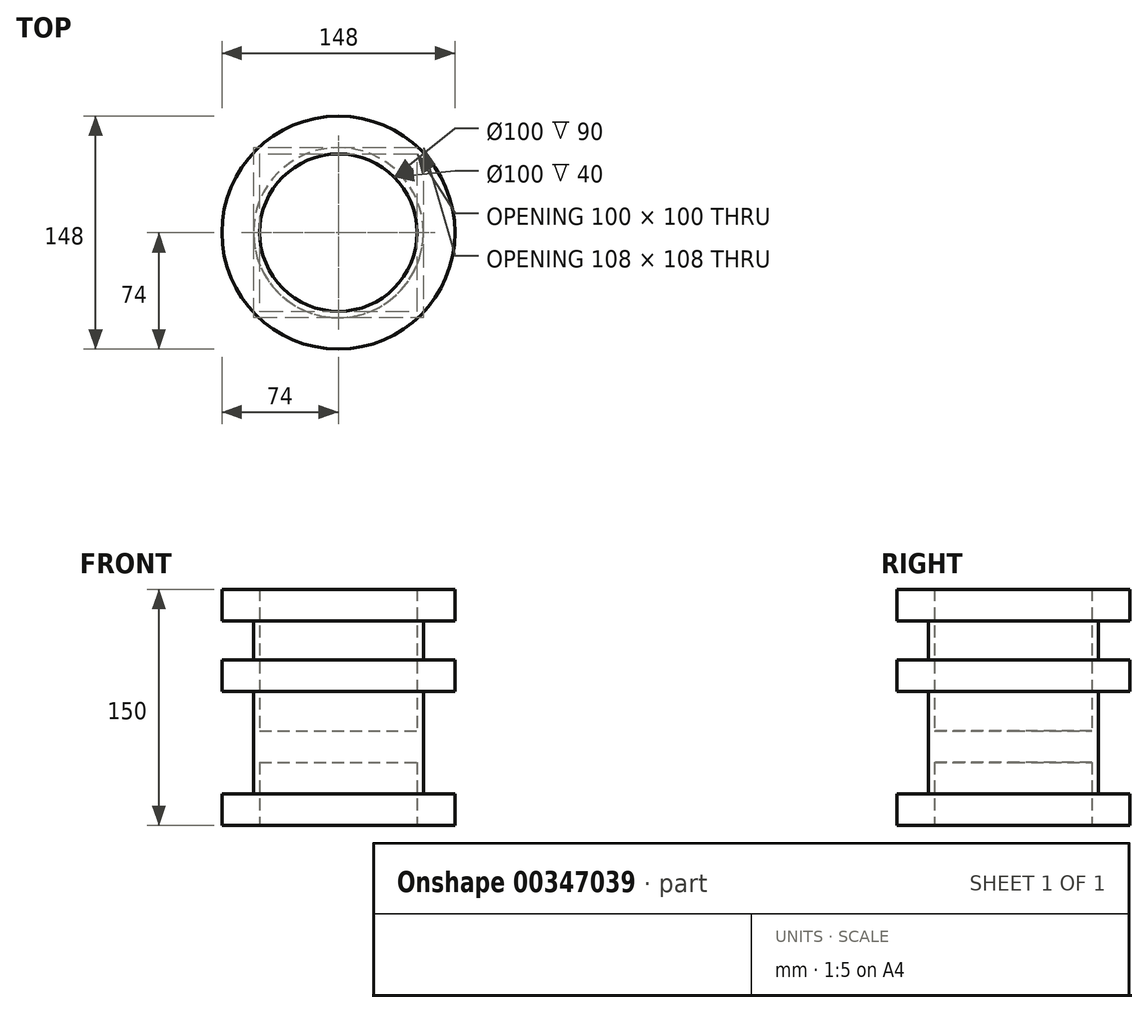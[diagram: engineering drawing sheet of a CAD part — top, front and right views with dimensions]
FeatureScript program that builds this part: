
annotation { "Feature Type Name" : "Feature", "Feature Type Description" : "" }
export const myFeature = defineFeature(function(context is Context, id is Id, definition is map)
    precondition{}
    {
        {
            var Q0;
            Q0=qCreatedBy(makeId("Top.planeOp"),FACE);
            var sketch = newSketch(context, id + "F0", { "sketchPlane" : qUnion([Q0])});
            skCircle(sketch, "E0", {"center": v(0, 0) * mm, "radius": 50 * mm});
            skCircle(sketch, "E1.0", {"center": v(0, 0) * mm, "radius": 54 * mm});
            skSolve(sketch);
        }
        {
            var Q0;
            Q0 = qSketchRegion(id + "F0", true);
            extrude(context, id + "F1", {"entities" : qUnion([Q0]), "depth" : 150 * mm});
        }
        {
            var Q0;
            Q0=qCreatedBy(makeId("Top.planeOp"),FACE);
            var sketch = newSketch(context, id + "F2", { "sketchPlane" : qUnion([Q0])});
            skCircle(sketch, "E2.0", {"center": v(0, 0) * mm, "radius": 54 * mm});
            skCircle(sketch, "E3.0", {"center": v(0, 0) * mm, "radius": 74 * mm});
            skSolve(sketch);
        }
        {
            var Q0;
            Q0=makeQuery(id+"F2.imprint","IMPRINT",FACE,{"disambiguationData":[TD([[makeQuery(id+"F2.imprint","IMPRINT",EDGE,{"derivedFrom":sQuery(id+"F2.wireOp",EDGE,"E2.0")}),-1.0]])]});
            extrude(context, id + "F3", {"entities" : qUnion([Q0]), "operationType" : NewBodyOperationType.ADD, "depth" : 20 * mm});
        }
        {
            var Q0;
            Q0=makeQuery(id+"F1.opExtrude","CAP_FACE",FACE,{"disambiguationData":[OSD([sQuery(id+"F0.wireOp",EDGE,"E0"),sQuery(id+"F0.wireOp",EDGE,"E1.0")])],"isStart":false});
            var sketch = newSketch(context, id + "F4", { "sketchPlane" : qUnion([Q0])});
            skCircle(sketch, "E4.0", {"center": v(0, 0) * mm, "radius": 54 * mm});
            skCircle(sketch, "E5.0", {"center": v(0, 0) * mm, "radius": 74 * mm});
            skSolve(sketch);
        }
        {
            var Q0;
            Q0=makeQuery(id+"F4.imprint","IMPRINT",FACE,{"disambiguationData":[TD([[makeQuery(id+"F4.imprint","IMPRINT",EDGE,{"derivedFrom":sQuery(id+"F4.wireOp",EDGE,"E4.0")}),-1.0]])]});
            extrude(context, id + "F5", {"entities" : qUnion([Q0]), "operationType" : NewBodyOperationType.ADD, "oppositeDirection" : true, "depth" : 20 * mm});
        }
        {
            var Q0;
            Q0=makeQuery(id+"F5.opExtrude","CAP_FACE",FACE,{"disambiguationData":[OSD([sQuery(id+"F4.wireOp",EDGE,"E4.0"),sQuery(id+"F4.wireOp",EDGE,"E5.0")])],"isStart":false});
            cPlane(context, id + "F6", {"entities" : qUnion([Q0]), "cplaneType" : CPlaneType.OFFSET, "offset" : 25 * mm, "width" : 150 * mm, "height" : 150 * mm});
        }
        {
            var Q0;
            Q0=qCreatedBy(id+"F6.planeOp",FACE);
            var sketch = newSketch(context, id + "F7", { "sketchPlane" : qUnion([Q0])});
            skCircle(sketch, "E6.0", {"center": v(0, 0) * mm, "radius": 54 * mm});
            skCircle(sketch, "E6.1", {"center": v(0, 0) * mm, "radius": 74 * mm});
            skSolve(sketch);
        }
        {
            var Q0;
            Q0 = qSketchRegion(id + "F7", true);
            extrude(context, id + "F8", {"entities" : qUnion([Q0]), "operationType" : NewBodyOperationType.ADD, "depth" : 20 * mm});
        }
        {
            var Q0;
            Q0=makeQuery(id+"F8.opExtrude","CAP_FACE",FACE,{"disambiguationData":[OSD([sQuery(id+"F7.wireOp",EDGE,"E6.0"),sQuery(id+"F7.wireOp",EDGE,"E6.1")])],"isStart":false});
            cPlane(context, id + "F9", {"entities" : qUnion([Q0]), "cplaneType" : CPlaneType.OFFSET, "offset" : 25 * mm, "width" : 150 * mm, "height" : 150 * mm});
        }
        {
            var Q0;
            Q0=qCreatedBy(id+"F9.planeOp",FACE);
            var sketch = newSketch(context, id + "F10", { "sketchPlane" : qUnion([Q0])});
            skCircle(sketch, "E7.0", {"center": v(0, 0) * mm, "radius": 54 * mm});
            skCircle(sketch, "E7.1", {"center": v(0, 0) * mm, "radius": 74 * mm});
            skSolve(sketch);
        }
        {
            var Q0;
            Q0=makeQuery(id+"F10.imprint","IMPRINT",FACE,{"disambiguationData":[TD([[makeQuery(id+"F10.imprint","IMPRINT",EDGE,{"derivedFrom":sQuery(id+"F10.wireOp",EDGE,"E7.0")}),1.0]])]});
            extrude(context, id + "F11", {"entities" : qUnion([Q0]), "operationType" : NewBodyOperationType.ADD, "depth" : 20 * mm});
        }
    });
